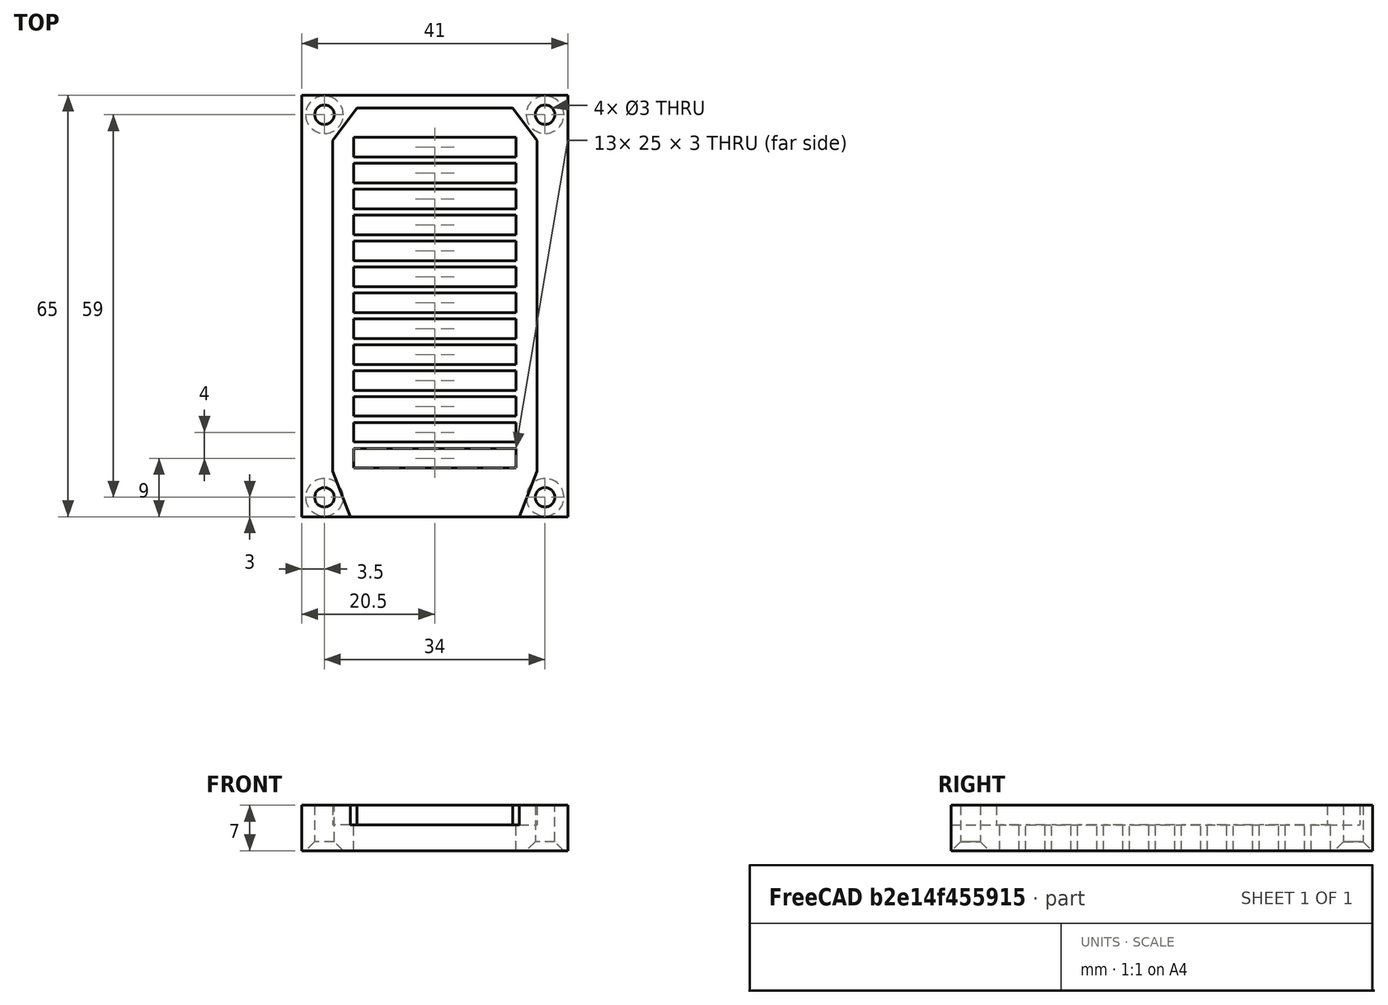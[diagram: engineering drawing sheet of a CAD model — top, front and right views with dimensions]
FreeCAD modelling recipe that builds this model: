
FCSTD DOCUMENT  (FreeCAD 0.18.1R)
Label: esp8266_temp_sensor_case_cover
License: All rights reserved
LicenseURL: http://en.wikipedia.org/wiki/All_rights_reserved
objects: Sketcher::SketchObject×3, PartDesign::Pocket×2, Part::Box×1, Part::FeaturePython×1, Mesh::Feature×1, PartDesign::Body×1, PartDesign::Pad×1, PartDesign::Chamfer×1, Part::Cut×1
note: 14 computed .brp shape members not serialized (recipe doc carries the construction recipe); baked Part::Feature solids carry a one-line shape summary decoded from their .brp

FEATURE [Sketcher::SketchObject] CopySketch001
  Placement = pos=(0,0,7) rot=(0,0,1;0rad)
  sketch-geometry (8):
    g0: LineSegment StartX=-12 StartY=30.5 StartZ=0 EndX=12 EndY=30.5 EndZ=0
    g1: LineSegment StartX=12 StartY=30.5 StartZ=0 EndX=15.75 EndY=25.5 EndZ=0
    g2: LineSegment StartX=15.75 StartY=25.5 StartZ=0 EndX=15.75 EndY=-25.5 EndZ=0
    g3: LineSegment StartX=-13 StartY=-32.5 StartZ=0 EndX=-15.75 EndY=-25.5 EndZ=0
    g4: LineSegment StartX=-15.75 StartY=-25.5 StartZ=0 EndX=-15.75 EndY=25.5 EndZ=0
    g5: LineSegment StartX=-15.75 StartY=25.5 StartZ=0 EndX=-12 EndY=30.5 EndZ=0
    g6: LineSegment StartX=15.75 StartY=-25.5 StartZ=0 EndX=13 EndY=-32.5 EndZ=0
    g7: LineSegment StartX=-13 StartY=-32.5 StartZ=0 EndX=13 EndY=-32.5 EndZ=0
  constraints (16):
    c: Coincident(g0,g1)
    c: Coincident(g1,g2)
    c: Coincident(g3,g4)
    c: Coincident(g4,g5)
    c: Coincident(g5,g0)
    c: DistanceX(g1) = 15.75
    c: DistanceY(g1) = 25.5
    c: DistanceX(g0) = 12
    c: DistanceY(g0) = 30.5
    c: Symmetric(g0,g0,g-2)
    c: Symmetric(g1,g4,g-2)
    c: Symmetric(g1,g2,g-1)
    c: DistanceX(g3) = -13
    c: DistanceY(g3) = -32.5
    c: Symmetric(g3,g6,g-2)
    c: Symmetric(g3,g2,g-2)
FEATURE [Part::Box] Box  label="Cube"
  AttacherType = Attacher::AttachEngine3D
  Height = 10
  Length = 25
  Placement = pos=(-12.5,-25,0) rot=(0,0,1;0rad)
  Width = 3
FEATURE [Part::FeaturePython] Array  # Draft array (typed FeaturePython)
  Angle = 360
  ArrayType = 0
  Axis = (0,0,1)
  Base = -> Box
  Center = (0,0,0)
  Fuse = false
  IntervalAxis = (0,0,0)
  IntervalX = (1,0,0)
  IntervalY = (0,4,0)
  IntervalZ = (0,0,1)
  NumberPolar = 1
  NumberX = 1
  NumberY = 13
  NumberZ = 1
FEATURE [Mesh::Feature] Mesh  label="Cut (Meshed)"
FEATURE [PartDesign::Body] Body
  Group = -> [Sketch,Pad,Pocket,Sketch002,Pocket001,Chamfer]
  Origin = -> Origin
  Tip = -> Chamfer
FEATURE [Sketcher::SketchObject] Sketch
  MapMode = 5
  Placement = pos=(0,0,4) rot=(0,0,1;0rad)
  Support = -> [Chamfer]
  sketch-geometry (4):
    g0: LineSegment StartX=-10 StartY=2 StartZ=0 EndX=10 EndY=2 EndZ=0
    g1: LineSegment StartX=10 StartY=2 StartZ=0 EndX=10 EndY=-2 EndZ=0
    g2: LineSegment StartX=10 StartY=-2 StartZ=0 EndX=-10 EndY=-2 EndZ=0
    g3: LineSegment StartX=-10 StartY=-2 StartZ=0 EndX=-10 EndY=2 EndZ=0
  constraints (11):
    c: Coincident(g0,g1)
    c: Coincident(g1,g2)
    c: Coincident(g2,g3)
    c: Coincident(g3,g0)
    c: Vertical(g1)
    c: Vertical(g3)
    c: DistanceX(g0) = 10
    c: DistanceY(g0) = 2
    c: Symmetric(g0,g2,g-1)
    c: Symmetric(g2,g1,g-2)
    c: Symmetric(g0,g0,g-2)
FEATURE [PartDesign::Pad] Pad
  Length = 7
  Length2 = 100
  Profile = -> Sketch
  Type = 0
FEATURE [PartDesign::Pocket] Pocket
  BaseFeature = -> Pad
  Length = 3
  Length2 = 100
  Profile = -> CopySketch001
  Type = 0
FEATURE [Sketcher::SketchObject] Sketch002
  MapMode = 5
  Placement = pos=(0,0,0) rot=(1,0,0;3.14159rad)
  Support = -> [Pocket]
  sketch-geometry (4):
    g0: Circle CenterX=17 CenterY=29.5 CenterZ=0 NormalX=0 NormalY=0 NormalZ=1 AngleXU=0 Radius=1.5
    g1: Circle CenterX=-17 CenterY=29.5 CenterZ=0 NormalX=0 NormalY=0 NormalZ=1 AngleXU=0 Radius=1.5
    g2: Circle CenterX=-17 CenterY=-29.5 CenterZ=0 NormalX=0 NormalY=0 NormalZ=1 AngleXU=0 Radius=1.5
    g3: Circle CenterX=17 CenterY=-29.5 CenterZ=0 NormalX=0 NormalY=0 NormalZ=1 AngleXU=0 Radius=1.5
  constraints (9):
    c: DistanceX(g0) = 17
    c: DistanceY(g0) = 29.5
    c: Radius(g0) = 1.5
    c: Equal(g0,g1) = 1.5
    c: Equal(g0,g2) = 1.5
    c: Equal(g0,g3) = 1.5
    c: Symmetric(g0,g1,g-2)
    c: Symmetric(g1,g2,g-1)
    c: Symmetric(g2,g3,g-2)
FEATURE [PartDesign::Pocket] Pocket001
  BaseFeature = -> Pocket
  Length = 10
  Length2 = 100
  Profile = -> Sketch002
  Type = 0
FEATURE [PartDesign::Chamfer] Chamfer
  Base = -> Pocket001 [Edge14,Edge13,Edge12,Edge15]
  BaseFeature = -> Pocket001
  Size = 1.4
FEATURE [Part::Cut] Cut
  Base = -> Body
  Tool = -> Array
